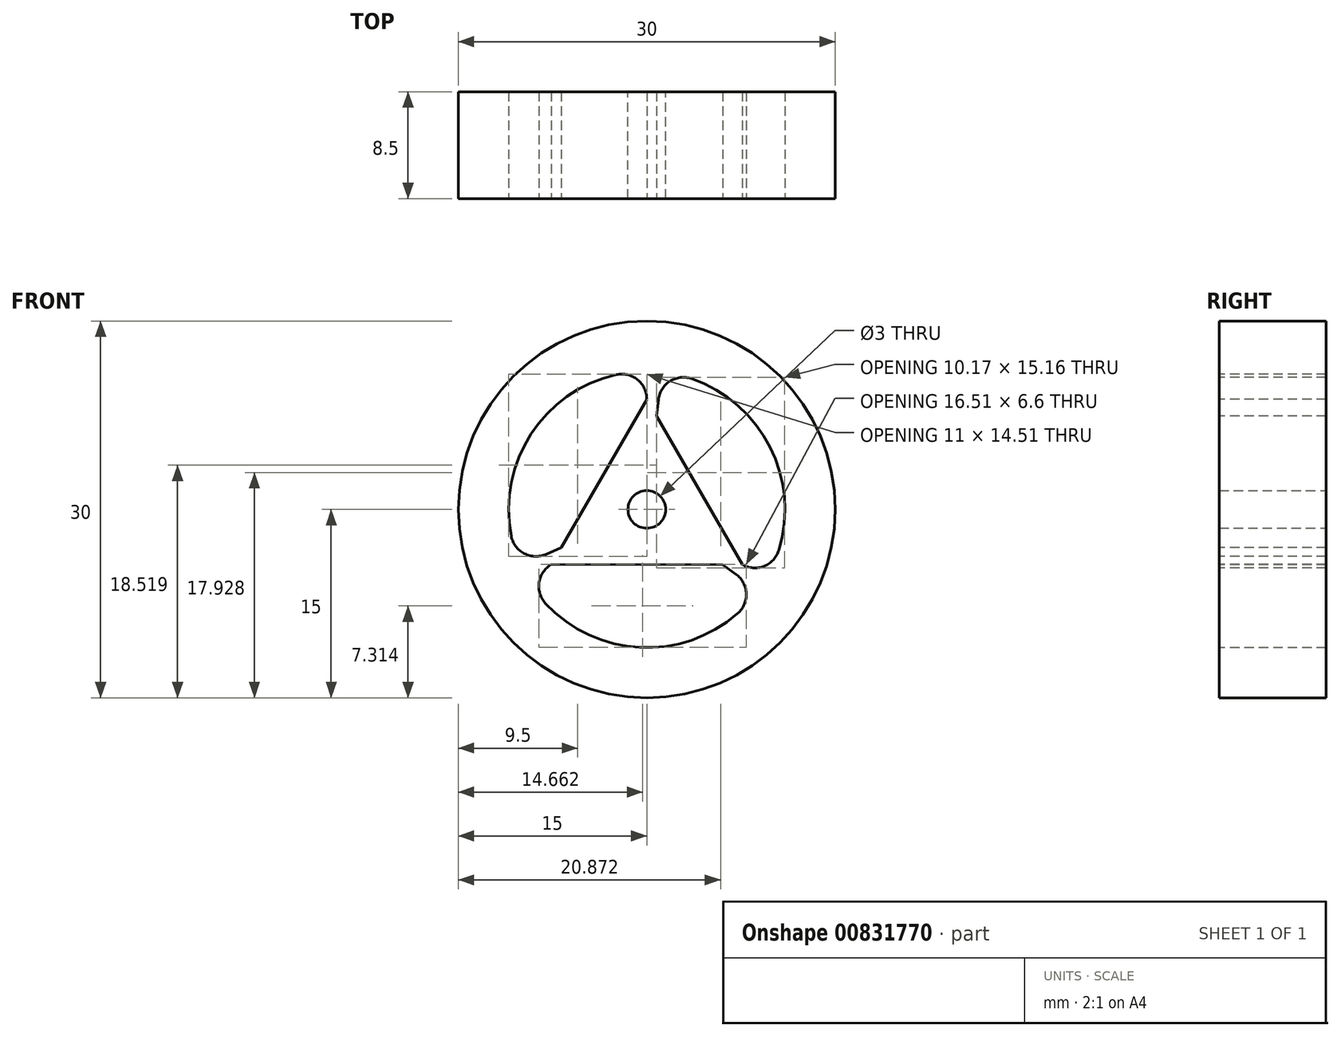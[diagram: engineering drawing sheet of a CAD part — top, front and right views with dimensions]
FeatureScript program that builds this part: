
annotation { "Feature Type Name" : "Feature", "Feature Type Description" : "" }
export const myFeature = defineFeature(function(context is Context, id is Id, definition is map)
    precondition{}
    {
        {
            var Q0;
            Q0=qCreatedBy(makeId("Front.planeOp"),FACE);
            var sketch = newSketch(context, id + "F0", { "sketchPlane" : qUnion([Q0])});
            skCircle(sketch, "E0", {"center": v(0, 0) * mm, "radius": 15 * mm});
            skCircle(sketch, "E1", {"center": v(0, 0) * mm, "radius": 1.5 * mm});
            skSolve(sketch);
        }
        {
            var Q0;
            Q0=makeQuery(id+"F0.imprint","IMPRINT",FACE,{"disambiguationData":[TD([[makeQuery(id+"F0.imprint","IMPRINT",EDGE,{"derivedFrom":sQuery(id+"F0.wireOp",EDGE,"E0")}),1.0]])]});
            extrude(context, id + "F1", {"entities" : qUnion([Q0]), "depth" : 8.5 * mm, "offsetDistance" : 25 * mm});
        }
        {
            var Q0;
            Q0=makeQuery(id+"F1.opExtrude","CAP_FACE",FACE,{"disambiguationData":[OSD([sQuery(id+"F0.wireOp",EDGE,"E0"),sQuery(id+"F0.wireOp",EDGE,"E1")])],"isStart":false});
            var sketch = newSketch(context, id + "F2", { "sketchPlane" : qUnion([Q0])});
            skLineSegment(sketch, "E2", {"start": v(-6.83, -3.04) * mm, "end": v(-8.02, -3.57) * mm});
            skArc(sketch, "E3", {"start": v(-2.44, 10.72) * mm, "mid": v(-9.22, 6) * mm, "end": v(-10.8, -2.12) * mm});
            skPoint(sketch, "E4.visualSharp", {"position": v(-10.05, -4.47) * mm});
            skArc(sketch, "E4.filletArc", {"start": v(-10.8, -2.12) * mm, "mid": v(-9.75, -3.51) * mm, "end": v(-8.02, -3.57) * mm});
            skPoint(sketch, "E5.visualSharp", {"position": v(0, 11) * mm});
            skArc(sketch, "E5.filletArc", {"start": v(0, 8.77) * mm, "mid": v(-0.75, 10.34) * mm, "end": v(-2.44, 10.72) * mm});
            skArc(sketch, "E6.1.0", {"start": v(-7.6, -4.39) * mm, "mid": v(-8.58, -5.82) * mm, "end": v(-8.07, -7.48) * mm});
            skArc(sketch, "E6.2.0", {"start": v(7.6, -4.39) * mm, "mid": v(9.33, -4.52) * mm, "end": v(10.51, -3.25) * mm});
            skArc(sketch, "E7.1.0", {"start": v(-8.07, -7.48) * mm, "mid": v(-0.58, -10.98) * mm, "end": v(7.24, -8.29) * mm});
            skArc(sketch, "E7.2.0", {"start": v(10.51, -3.25) * mm, "mid": v(9.8, 5) * mm, "end": v(3.56, 10.4) * mm});
            skArc(sketch, "E8.1.0", {"start": v(7.24, -8.29) * mm, "mid": v(7.92, -6.69) * mm, "end": v(7.1, -5.16) * mm});
            skArc(sketch, "E8.2.0", {"start": v(3.56, 10.4) * mm, "mid": v(1.83, 10.2) * mm, "end": v(0.92, 8.73) * mm});
            skLineSegment(sketch, "E9.1.0", {"start": v(6.04, -4.4) * mm, "end": v(7.1, -5.16) * mm});
            skLineSegment(sketch, "E9.2.0", {"start": v(0.78, 7.43) * mm, "end": v(0.92, 8.73) * mm});
            skLineSegment(sketch, "E10", {"start": v(-6.83, -3.04) * mm, "end": v(0, 8.77) * mm});
            skLineSegment(sketch, "E11", {"start": v(0.78, 7.43) * mm, "end": v(7.6, -4.39) * mm});
            skLineSegment(sketch, "E12", {"start": v(6.04, -4.4) * mm, "end": v(-7.6, -4.39) * mm});
            skSolve(sketch);
        }
        {
            var Q0;
            Q0=makeQuery(id+"F2.imprint","IMPRINT",FACE,{"disambiguationData":[TD([[makeQuery(id+"F2.imprint","IMPRINT",EDGE,{"derivedFrom":sQuery(id+"F2.wireOp",EDGE,"E2")}),-1.0]])]});
            var Q1;
            Q1=makeQuery(id+"F2.imprint","IMPRINT",FACE,{"disambiguationData":[TD([[makeQuery(id+"F2.imprint","IMPRINT",EDGE,{"derivedFrom":sQuery(id+"F2.wireOp",EDGE,"E6.2.0")}),1.0]])]});
            var Q2;
            Q2=makeQuery(id+"F2.imprint","IMPRINT",FACE,{"disambiguationData":[TD([[makeQuery(id+"F2.imprint","IMPRINT",EDGE,{"derivedFrom":sQuery(id+"F2.wireOp",EDGE,"E6.1.0")}),1.0]])]});
            extrude(context, id + "F3", {"entities" : qUnion([Q0, Q1, Q2]), "operationType" : NewBodyOperationType.REMOVE, "endBound" : BoundingType.THROUGH_ALL, "oppositeDirection" : true, "depth" : 25 * mm, "offsetDistance" : 25 * mm});
        }
    });
